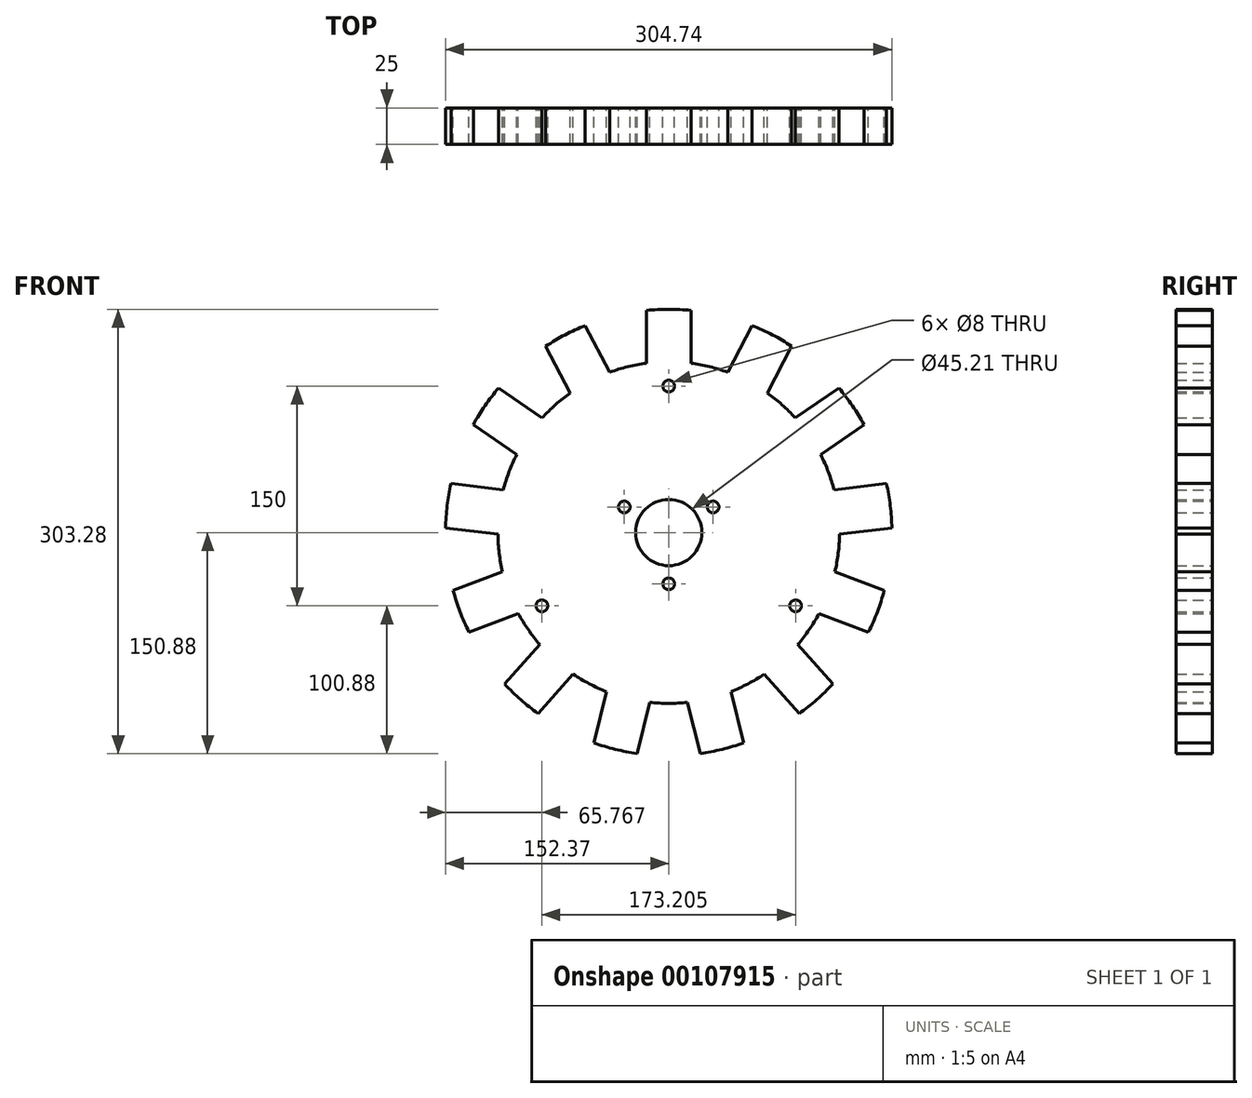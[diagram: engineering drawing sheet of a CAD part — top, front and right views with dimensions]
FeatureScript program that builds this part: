
annotation { "Feature Type Name" : "Feature", "Feature Type Description" : "" }
export const myFeature = defineFeature(function(context is Context, id is Id, definition is map)
    precondition{}
    {
        {
            var Q0;
            Q0=qCreatedBy(makeId("Front.planeOp"),FACE);
            var sketch = newSketch(context, id + "F0", { "sketchPlane" : qUnion([Q0])});
            skLineSegment(sketch, "E0", {"start": v(0, 0) * mm, "end": v(0, 152.4) * mm, "construction": true});
            skLineSegment(sketch, "E1", {"start": v(-15.24, 115.6) * mm, "end": v(-15.24, 151.64) * mm});
            skArc(sketch, "E2.trimOffspring", {"start": v(15.24, 151.64) * mm, "mid": v(0, 152.4) * mm, "end": v(-15.24, 151.64) * mm});
            skCircle(sketch, "E3", {"center": v(0, 0) * mm, "radius": 22.6 * mm});
            skCircle(sketch, "E4", {"center": v(0, 100) * mm, "radius": 4 * mm});
            skCircle(sketch, "E5", {"center": v(0, -35) * mm, "radius": 4 * mm});
            skCircle(sketch, "E6.1.0", {"center": v(-86.6, -50) * mm, "radius": 4 * mm});
            skCircle(sketch, "E6.2.0", {"center": v(86.6, -50) * mm, "radius": 4 * mm});
            skCircle(sketch, "E7.1.0", {"center": v(30.31, 17.5) * mm, "radius": 4 * mm});
            skCircle(sketch, "E7.2.0", {"center": v(-30.31, 17.5) * mm, "radius": 4 * mm});
            skCircle(sketch, "E8", {"center": v(0, 0) * mm, "radius": 92.5 * mm, "construction": true});
            skLineSegment(sketch, "E9", {"start": v(0, 0) * mm, "end": v(-15.13, 91.25) * mm, "construction": true});
            skLineSegment(sketch, "E10", {"start": v(0, 0) * mm, "end": v(15.13, 91.25) * mm, "construction": true});
            skArc(sketch, "E11", {"start": v(-15.24, 115.6) * mm, "mid": v(-27.9, 113.22) * mm, "end": v(-40.23, 109.45) * mm});
            skLineSegment(sketch, "E12", {"start": v(15.24, 151.64) * mm, "end": v(15.24, 115.6) * mm});
            skLineSegment(sketch, "E13.1.0", {"start": v(-67.22, 95.28) * mm, "end": v(-83.96, 127.18) * mm});
            skArc(sketch, "E13.1.1", {"start": v(-56.97, 141.35) * mm, "mid": v(-70.82, 134.94) * mm, "end": v(-83.96, 127.18) * mm});
            skLineSegment(sketch, "E13.1.2", {"start": v(-56.97, 141.35) * mm, "end": v(-40.23, 109.45) * mm});
            skLineSegment(sketch, "E13.2.0", {"start": v(-103.8, 53.13) * mm, "end": v(-133.45, 73.6) * mm});
            skArc(sketch, "E13.2.1", {"start": v(-116.14, 98.68) * mm, "mid": v(-125.42, 86.57) * mm, "end": v(-133.45, 73.6) * mm});
            skLineSegment(sketch, "E13.2.2", {"start": v(-116.14, 98.68) * mm, "end": v(-86.49, 78.21) * mm});
            skLineSegment(sketch, "E13.3.0", {"start": v(-116.6, -1.2) * mm, "end": v(-152.37, 3.15) * mm});
            skArc(sketch, "E13.3.1", {"start": v(-148.7, 33.4) * mm, "mid": v(-151.29, 18.37) * mm, "end": v(-152.37, 3.15) * mm});
            skLineSegment(sketch, "E13.3.2", {"start": v(-148.7, 33.4) * mm, "end": v(-112.93, 29.06) * mm});
            skLineSegment(sketch, "E13.4.0", {"start": v(-102.69, -55.24) * mm, "end": v(-136.38, -68.02) * mm});
            skArc(sketch, "E13.4.1", {"start": v(-147.19, -39.52) * mm, "mid": v(-142.5, -54.04) * mm, "end": v(-136.38, -68.02) * mm});
            skLineSegment(sketch, "E13.4.2", {"start": v(-147.19, -39.52) * mm, "end": v(-113.5, -26.75) * mm});
            skLineSegment(sketch, "E13.5.0", {"start": v(-65.25, -96.64) * mm, "end": v(-89.15, -123.6) * mm});
            skArc(sketch, "E13.5.1", {"start": v(-111.96, -103.4) * mm, "mid": v(-101.06, -114.07) * mm, "end": v(-89.15, -123.6) * mm});
            skLineSegment(sketch, "E13.5.2", {"start": v(-111.96, -103.4) * mm, "end": v(-88.07, -76.43) * mm});
            skLineSegment(sketch, "E13.6.0", {"start": v(-12.87, -115.9) * mm, "end": v(-21.5, -150.88) * mm});
            skArc(sketch, "E13.6.1", {"start": v(-51.09, -143.58) * mm, "mid": v(-36.47, -147.97) * mm, "end": v(-21.5, -150.88) * mm});
            skLineSegment(sketch, "E13.6.2", {"start": v(-51.09, -143.58) * mm, "end": v(-42.46, -108.6) * mm});
            skLineSegment(sketch, "E13.7.0", {"start": v(42.46, -108.6) * mm, "end": v(51.09, -143.58) * mm});
            skArc(sketch, "E13.7.1", {"start": v(21.5, -150.88) * mm, "mid": v(36.47, -147.97) * mm, "end": v(51.09, -143.58) * mm});
            skLineSegment(sketch, "E13.7.2", {"start": v(21.5, -150.88) * mm, "end": v(12.87, -115.9) * mm});
            skLineSegment(sketch, "E13.8.0", {"start": v(88.07, -76.43) * mm, "end": v(111.96, -103.4) * mm});
            skArc(sketch, "E13.8.1", {"start": v(89.15, -123.6) * mm, "mid": v(101.06, -114.07) * mm, "end": v(111.96, -103.4) * mm});
            skLineSegment(sketch, "E13.8.2", {"start": v(89.15, -123.6) * mm, "end": v(65.25, -96.64) * mm});
            skLineSegment(sketch, "E13.9.0", {"start": v(113.5, -26.75) * mm, "end": v(147.19, -39.52) * mm});
            skArc(sketch, "E13.9.1", {"start": v(136.38, -68.02) * mm, "mid": v(142.5, -54.04) * mm, "end": v(147.19, -39.52) * mm});
            skLineSegment(sketch, "E13.9.2", {"start": v(136.38, -68.02) * mm, "end": v(102.69, -55.24) * mm});
            skLineSegment(sketch, "E13.10.0", {"start": v(112.93, 29.06) * mm, "end": v(148.7, 33.4) * mm});
            skArc(sketch, "E13.10.1", {"start": v(152.37, 3.15) * mm, "mid": v(151.29, 18.37) * mm, "end": v(148.7, 33.4) * mm});
            skLineSegment(sketch, "E13.10.2", {"start": v(152.37, 3.15) * mm, "end": v(116.6, -1.2) * mm});
            skLineSegment(sketch, "E13.11.0", {"start": v(86.49, 78.21) * mm, "end": v(116.14, 98.68) * mm});
            skArc(sketch, "E13.11.1", {"start": v(133.45, 73.6) * mm, "mid": v(125.42, 86.57) * mm, "end": v(116.14, 98.68) * mm});
            skLineSegment(sketch, "E13.11.2", {"start": v(133.45, 73.6) * mm, "end": v(103.8, 53.13) * mm});
            skLineSegment(sketch, "E13.12.0", {"start": v(40.23, 109.45) * mm, "end": v(56.97, 141.35) * mm});
            skArc(sketch, "E13.12.1", {"start": v(83.96, 127.18) * mm, "mid": v(70.82, 134.94) * mm, "end": v(56.97, 141.35) * mm});
            skLineSegment(sketch, "E13.12.2", {"start": v(83.96, 127.18) * mm, "end": v(67.22, 95.28) * mm});
            skArc(sketch, "E14.trimOffspring", {"start": v(40.23, 109.45) * mm, "mid": v(27.9, 113.22) * mm, "end": v(15.24, 115.6) * mm});
            skArc(sketch, "E15.trimOffspring", {"start": v(86.49, 78.21) * mm, "mid": v(77.32, 87.28) * mm, "end": v(67.22, 95.28) * mm});
            skArc(sketch, "E16.trimOffspring", {"start": v(112.93, 29.06) * mm, "mid": v(109.03, 41.35) * mm, "end": v(103.8, 53.13) * mm});
            skArc(sketch, "E17.trimOffspring", {"start": v(113.5, -26.75) * mm, "mid": v(115.76, -14.06) * mm, "end": v(116.6, -1.2) * mm});
            skArc(sketch, "E18.trimOffspring", {"start": v(-67.22, 95.28) * mm, "mid": v(-77.32, 87.28) * mm, "end": v(-86.49, 78.21) * mm});
            skArc(sketch, "E19.trimOffspring", {"start": v(-103.8, 53.13) * mm, "mid": v(-109.03, 41.35) * mm, "end": v(-112.93, 29.06) * mm});
            skArc(sketch, "E20.trimOffspring", {"start": v(-116.6, -1.2) * mm, "mid": v(-115.76, -14.06) * mm, "end": v(-113.5, -26.75) * mm});
            skArc(sketch, "E21.trimOffspring", {"start": v(-102.69, -55.24) * mm, "mid": v(-95.97, -66.24) * mm, "end": v(-88.07, -76.43) * mm});
            skArc(sketch, "E22.trimOffspring", {"start": v(-65.25, -96.64) * mm, "mid": v(-54.19, -103.25) * mm, "end": v(-42.46, -108.6) * mm});
            skArc(sketch, "E23.trimOffspring", {"start": v(-12.87, -115.9) * mm, "mid": v(0, -116.6) * mm, "end": v(12.87, -115.9) * mm});
            skArc(sketch, "E24.trimOffspring", {"start": v(42.46, -108.6) * mm, "mid": v(54.19, -103.25) * mm, "end": v(65.25, -96.64) * mm});
            skArc(sketch, "E25.trimOffspring", {"start": v(88.07, -76.43) * mm, "mid": v(95.97, -66.24) * mm, "end": v(102.69, -55.24) * mm});
            skCircle(sketch, "E26", {"center": v(0, 0) * mm, "radius": 150 * mm, "construction": true});
            skSolve(sketch);
        }
        {
            var Q0;
            Q0 = qSketchRegion(id + "F0", true);
            extrude(context, id + "F1", {"entities" : qUnion([Q0]), "depth" : 25 * mm, "offsetDistance" : 25 * mm});
        }
    });
